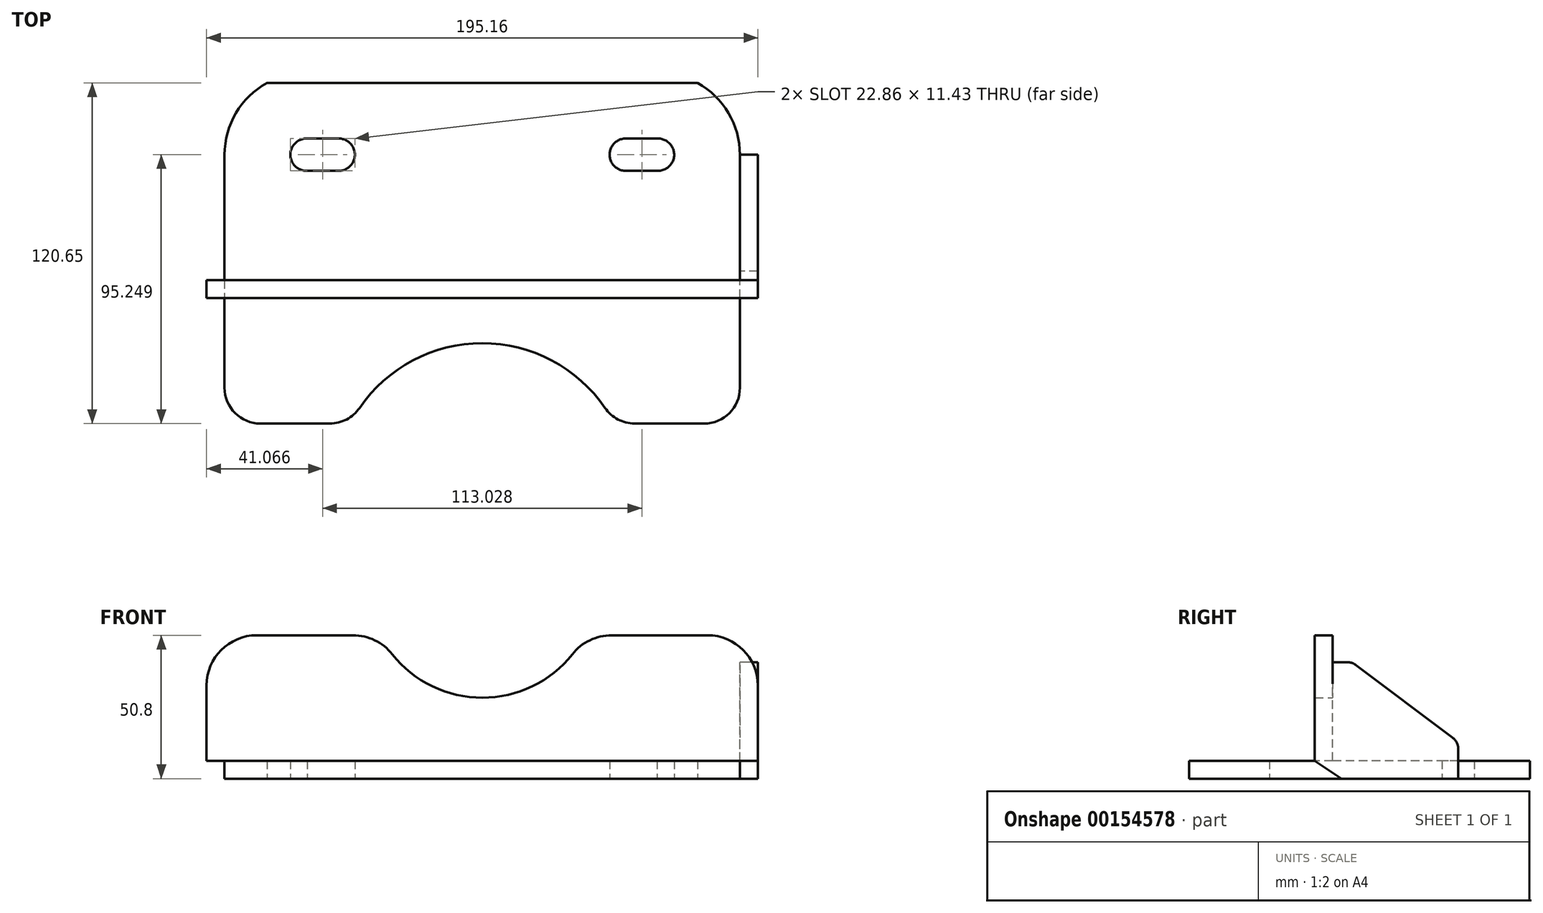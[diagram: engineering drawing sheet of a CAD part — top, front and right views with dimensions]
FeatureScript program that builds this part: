
annotation { "Feature Type Name" : "Feature", "Feature Type Description" : "" }
export const myFeature = defineFeature(function(context is Context, id is Id, definition is map)
    precondition{}
    {
        {
            var Q0;
            Q0=qCreatedBy(makeId("Top.planeOp"),FACE);
            var sketch = newSketch(context, id + "F0", { "sketchPlane" : qUnion([Q0])});
            skLineSegment(sketch, "E0.top", {"start": v(0, 80.17) * mm, "end": v(152.4, 80.17) * mm});
            skArc(sketch, "E1", {"start": v(25.4, 49.05) * mm, "mid": v(31.11, 54.77) * mm, "end": v(25.4, 60.48) * mm});
            skArc(sketch, "E2", {"start": v(13.97, 60.48) * mm, "mid": v(8.26, 54.62) * mm, "end": v(14.26, 49.06) * mm});
            skLineSegment(sketch, "E3", {"start": v(14.26, 49.06) * mm, "end": v(25.4, 49.05) * mm});
            skLineSegment(sketch, "E4", {"start": v(13.97, 60.48) * mm, "end": v(25.4, 60.48) * mm});
            skPoint(sketch, "E5.center.orphan", {"position": v(19.68, 54.77) * mm});
            skPoint(sketch, "E6.MirrorP", {"position": v(132.72, 54.77) * mm});
            skArc(sketch, "E7.MirrorCS", {"start": v(127, 49.05) * mm, "mid": v(121.29, 54.77) * mm, "end": v(127, 60.48) * mm});
            skLineSegment(sketch, "E8.MirrorCS", {"start": v(138.14, 49.06) * mm, "end": v(127, 49.05) * mm});
            skLineSegment(sketch, "E9.MirrorCS", {"start": v(138.43, 60.48) * mm, "end": v(127, 60.48) * mm});
            skArc(sketch, "E10.MirrorCS", {"start": v(138.43, 60.48) * mm, "mid": v(144.14, 54.62) * mm, "end": v(138.14, 49.06) * mm});
            skArc(sketch, "E11", {"start": v(0, 80.17) * mm, "mid": v(-10.98, 69.52) * mm, "end": v(-15.02, 54.77) * mm});
            skArc(sketch, "E12", {"start": v(167.42, 54.77) * mm, "mid": v(163.38, 69.52) * mm, "end": v(152.4, 80.17) * mm});
            skPoint(sketch, "E13.start.orphan", {"position": v(76.2, 80.17) * mm});
            skLineSegment(sketch, "E14", {"start": v(-15.02, 54.77) * mm, "end": v(-15.02, 3.97) * mm});
            skLineSegment(sketch, "E15", {"start": v(167.42, 54.77) * mm, "end": v(167.42, 3.97) * mm});
            skLineSegment(sketch, "E16.MirrorCS", {"start": v(63.25, 10.32) * mm, "end": v(63.25, 3.97) * mm});
            skPoint(sketch, "E17.orphan", {"position": v(76.2, 3.97) * mm});
            skLineSegment(sketch, "E18", {"start": v(63.25, 10.32) * mm, "end": v(89.15, 10.32) * mm});
            skLineSegment(sketch, "E19", {"start": v(89.15, 3.97) * mm, "end": v(89.15, 10.32) * mm});
            skLineSegment(sketch, "E20", {"start": v(63.25, 3.97) * mm, "end": v(89.15, 3.97) * mm});
            skLineSegment(sketch, "E21", {"start": v(-15.02, 3.97) * mm, "end": v(-15.02, -27.78) * mm});
            skLineSegment(sketch, "E22", {"start": v(167.42, 3.97) * mm, "end": v(167.42, -27.78) * mm});
            skPoint(sketch, "E23.visualSharp", {"position": v(-15.02, -40.48) * mm});
            skArc(sketch, "E23.filletArc", {"start": v(-15.02, -27.78) * mm, "mid": v(-11.3, -36.76) * mm, "end": v(-2.32, -40.48) * mm});
            skPoint(sketch, "E24.visualSharp", {"position": v(167.42, -40.48) * mm});
            skArc(sketch, "E24.filletArc", {"start": v(154.72, -40.48) * mm, "mid": v(163.7, -36.76) * mm, "end": v(167.42, -27.78) * mm});
            skLineSegment(sketch, "E25", {"start": v(76.2, 3.97) * mm, "end": v(76.2, -26.95) * mm});
            skLineSegment(sketch, "E26", {"start": v(-2.32, -40.48) * mm, "end": v(22.26, -40.48) * mm});
            skLineSegment(sketch, "E27", {"start": v(154.72, -40.48) * mm, "end": v(130.14, -40.48) * mm});
            skArc(sketch, "E28", {"start": v(119.66, -34.95) * mm, "mid": v(76.2, -12.03) * mm, "end": v(32.74, -34.95) * mm});
            skPoint(sketch, "E29.visualSharp", {"position": v(29.43, -40.48) * mm});
            skArc(sketch, "E29.filletArc", {"start": v(22.26, -40.48) * mm, "mid": v(28.18, -39.01) * mm, "end": v(32.74, -34.95) * mm});
            skPoint(sketch, "E30.visualSharp", {"position": v(122.97, -40.48) * mm});
            skArc(sketch, "E30.filletArc", {"start": v(119.66, -34.95) * mm, "mid": v(124.22, -39.01) * mm, "end": v(130.14, -40.48) * mm});
            skSolve(sketch);
        }
        {
            var Q0;
            Q0 = qSketchRegion(id + "F0", true);
            extrude(context, id + "F1", {"entities" : qUnion([Q0]), "depth" : 6.35 * mm});
        }
        {
            var Q0;
            Q0=makeQuery(id+"F1.opExtrude","SWEPT_FACE",FACE,{"disambiguationData":[OSD([sQuery(id+"F0.wireOp",EDGE,"E18")])]});
            var sketch = newSketch(context, id + "F2", { "sketchPlane" : qUnion([Q0])});
            skLineSegment(sketch, "E31", {"start": v(63.25, 0) * mm, "end": v(63.25, 6.35) * mm});
            skLineSegment(sketch, "E32", {"start": v(63.25, 0) * mm, "end": v(76.2, 0) * mm});
            skLineSegment(sketch, "E33", {"start": v(63.25, 6.35) * mm, "end": v(-15.02, 6.35) * mm});
            skLineSegment(sketch, "E34", {"start": v(-15.02, 6.35) * mm, "end": v(-21.38, 6.35) * mm});
            skLineSegment(sketch, "E35", {"start": v(-21.38, 6.35) * mm, "end": v(-21.38, 33.02) * mm});
            skLineSegment(sketch, "E36.MirrorCS", {"start": v(173.78, 6.35) * mm, "end": v(173.78, 33.02) * mm});
            skLineSegment(sketch, "E37.MirrorCS", {"start": v(89.15, 6.35) * mm, "end": v(167.42, 6.35) * mm});
            skLineSegment(sketch, "E38.MirrorCS", {"start": v(167.42, 6.35) * mm, "end": v(173.78, 6.35) * mm});
            skLineSegment(sketch, "E39", {"start": v(-3.6, 50.8) * mm, "end": v(30.43, 50.8) * mm});
            skLineSegment(sketch, "E40.MirrorCS", {"start": v(89.15, 0) * mm, "end": v(89.15, 6.35) * mm});
            skLineSegment(sketch, "E41.MirrorCS", {"start": v(89.15, 0) * mm, "end": v(76.2, 0) * mm});
            skPoint(sketch, "E42.visualSharp", {"position": v(-21.38, 50.8) * mm});
            skArc(sketch, "E42.filletArc", {"start": v(-3.6, 50.8) * mm, "mid": v(-16.17, 45.6) * mm, "end": v(-21.38, 33.02) * mm});
            skPoint(sketch, "E43.visualSharp", {"position": v(173.78, 50.8) * mm});
            skArc(sketch, "E43.filletArc", {"start": v(173.78, 33.02) * mm, "mid": v(168.57, 45.6) * mm, "end": v(156, 50.8) * mm});
            skArc(sketch, "E44", {"start": v(44.37, 44.06) * mm, "mid": v(76.23, 28.65) * mm, "end": v(108.1, 44.06) * mm});
            skLineSegment(sketch, "E45.trimOffspring", {"start": v(122.03, 50.8) * mm, "end": v(156, 50.8) * mm});
            skPoint(sketch, "E46.visualSharp", {"position": v(40.04, 50.8) * mm});
            skArc(sketch, "E46.filletArc", {"start": v(44.37, 44.06) * mm, "mid": v(38.17, 49.03) * mm, "end": v(30.43, 50.8) * mm});
            skPoint(sketch, "E47.visualSharp", {"position": v(112.43, 50.8) * mm});
            skArc(sketch, "E47.filletArc", {"start": v(122.03, 50.8) * mm, "mid": v(114.3, 49.03) * mm, "end": v(108.1, 44.06) * mm});
            skSolve(sketch);
        }
        {
            var Q0;
            Q0 = qSketchRegion(id + "F2", true);
            extrude(context, id + "F3", {"entities" : qUnion([Q0]), "operationType" : NewBodyOperationType.ADD, "depth" : 6.35 * mm});
        }
        {
            var Q0;
            Q0=makeQuery(id+"F1.opExtrude","SWEPT_FACE",FACE,{"disambiguationData":[OSD([sQuery(id+"F0.wireOp",EDGE,"E15"),sQuery(id+"F0.wireOp",EDGE,"54778f9c-75b0-4388-bbda-856c98a165d10.MirrorCS")])]});
            var sketch = newSketch(context, id + "F4", { "sketchPlane" : qUnion([Q0])});
            skLineSegment(sketch, "E48", {"start": v(54.77, 0) * mm, "end": v(54.77, 10.46) * mm});
            skLineSegment(sketch, "E49", {"start": v(3.97, 6.35) * mm, "end": v(13.5, 0) * mm});
            skLineSegment(sketch, "E50", {"start": v(13.5, 0) * mm, "end": v(54.77, 0) * mm});
            skLineSegment(sketch, "E51", {"start": v(3.97, 6.35) * mm, "end": v(10.32, 6.35) * mm});
            skLineSegment(sketch, "E52", {"start": v(10.32, 6.35) * mm, "end": v(10.32, 41.25) * mm});
            skLineSegment(sketch, "E53", {"start": v(10.32, 41.25) * mm, "end": v(15.5, 41.25) * mm});
            skLineSegment(sketch, "E54", {"start": v(18.55, 40.23) * mm, "end": v(52.74, 14.52) * mm});
            skPoint(sketch, "E55.visualSharp", {"position": v(17.2, 41.25) * mm});
            skArc(sketch, "E55.filletArc", {"start": v(18.55, 40.23) * mm, "mid": v(17.1, 40.99) * mm, "end": v(15.5, 41.25) * mm});
            skPoint(sketch, "E56.visualSharp", {"position": v(54.77, 13) * mm});
            skArc(sketch, "E56.filletArc", {"start": v(54.77, 10.46) * mm, "mid": v(54.23, 12.73) * mm, "end": v(52.74, 14.52) * mm});
            skSolve(sketch);
        }
        {
            var Q0;
            Q0 = qSketchRegion(id + "F4", true);
            extrude(context, id + "F5", {"entities" : qUnion([Q0]), "operationType" : NewBodyOperationType.ADD, "depth" : 6.35 * mm});
        }
    });
